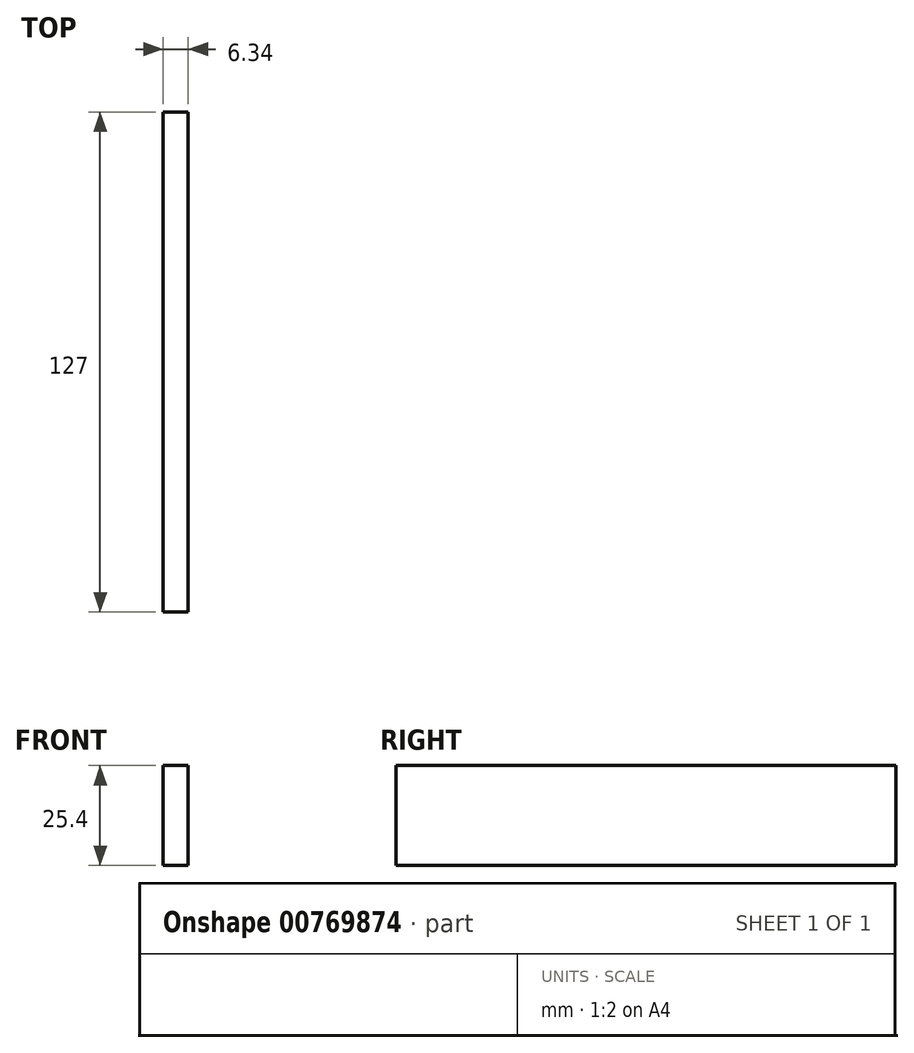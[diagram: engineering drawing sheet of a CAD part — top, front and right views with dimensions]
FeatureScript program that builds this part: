
annotation { "Feature Type Name" : "Feature", "Feature Type Description" : "" }
export const myFeature = defineFeature(function(context is Context, id is Id, definition is map)
    precondition{}
    {
        {
            var Q0;
            Q0=qCreatedBy(makeId("Top.planeOp"),FACE);
            var sketch = newSketch(context, id + "F0", { "sketchPlane" : qUnion([Q0])});
            skLineSegment(sketch, "E0.bottom", {"start": v(-3.17, 63.5) * mm, "end": v(3.18, 63.5) * mm});
            skLineSegment(sketch, "E0.top", {"start": v(-3.18, -63.5) * mm, "end": v(3.17, -63.5) * mm});
            skLineSegment(sketch, "E0.left", {"start": v(-3.17, 63.5) * mm, "end": v(-3.18, -63.5) * mm});
            skLineSegment(sketch, "E0.right", {"start": v(3.18, 63.5) * mm, "end": v(3.17, -63.5) * mm});
            skLineSegment(sketch, "E1", {"start": v(-3.17, 63.5) * mm, "end": v(3.17, -63.5) * mm, "construction": true});
            skSolve(sketch);
        }
        {
            var Q0;
            Q0 = qSketchRegion(id + "F0", true);
            extrude(context, id + "F1", {"entities" : qUnion([Q0]), "oppositeDirection" : true, "depth" : 25.4 * mm, "offsetDistance" : 25.4 * mm});
        }
    });
